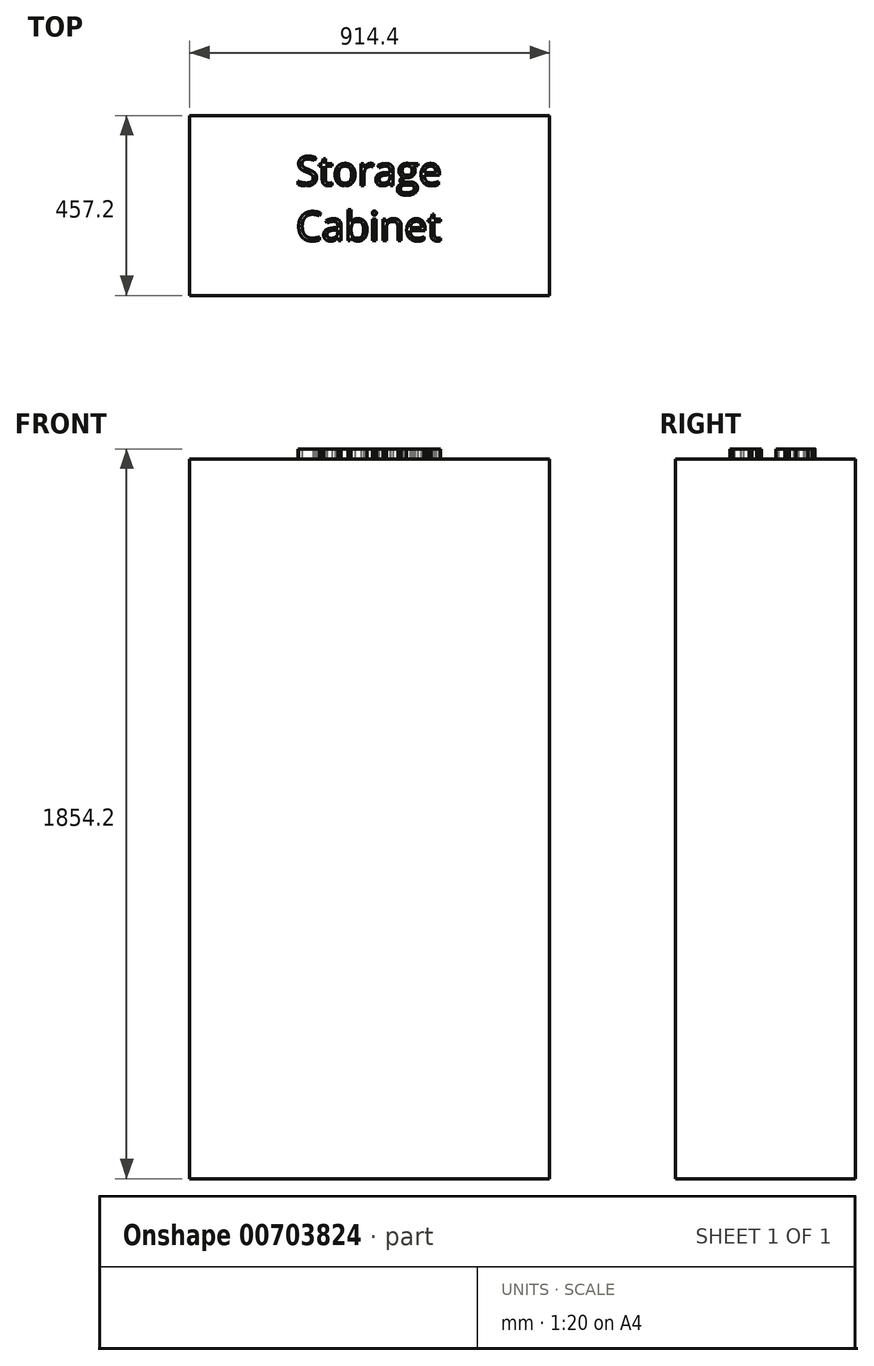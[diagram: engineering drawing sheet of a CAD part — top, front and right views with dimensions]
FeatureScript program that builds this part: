
annotation { "Feature Type Name" : "Feature", "Feature Type Description" : "" }
export const myFeature = defineFeature(function(context is Context, id is Id, definition is map)
    precondition{}
    {
        {
            var Q0;
            Q0=qCreatedBy(makeId("Top.planeOp"),FACE);
            var sketch = newSketch(context, id + "F0", { "sketchPlane" : qUnion([Q0])});
            skLineSegment(sketch, "E0.bottom", {"start": v(457.2, -228.6) * mm, "end": v(-457.2, -228.6) * mm});
            skLineSegment(sketch, "E0.top", {"start": v(457.2, 228.6) * mm, "end": v(-457.2, 228.6) * mm});
            skLineSegment(sketch, "E0.left", {"start": v(457.2, -228.6) * mm, "end": v(457.2, 228.6) * mm});
            skLineSegment(sketch, "E0.right", {"start": v(-457.2, -228.6) * mm, "end": v(-457.2, 228.6) * mm});
            skPoint(sketch, "E0.middle", {"position": v(0, 0) * mm});
            skSolve(sketch);
        }
        {
            var Q0;
            Q0=makeQuery(id+"F0.imprint","IMPRINT",FACE,{"disambiguationData":[TD([[makeQuery(id+"F0.imprint","IMPRINT",EDGE,{"derivedFrom":sQuery(id+"F0.wireOp",EDGE,"E0.bottom")}),-1.0]])]});
            extrude(context, id + "F1", {"entities" : qUnion([Q0]), "depth" : 1828.8 * mm, "offsetDistance" : 25.4 * mm});
        }
        {
            var Q0;
            Q0=makeQuery(id+"F1.opExtrude","CAP_FACE",FACE,{"disambiguationData":[OSD([sQuery(id+"F0.wireOp",EDGE,"E0.bottom"),sQuery(id+"F0.wireOp",EDGE,"E0.top"),sQuery(id+"F0.wireOp",EDGE,"E0.left"),sQuery(id+"F0.wireOp",EDGE,"E0.right")])],"isStart":false});
            var sketch = newSketch(context, id + "F2", { "sketchPlane" : qUnion([Q0])});
            skText(sketch, "E1", { "text": "Storage \nCabinet", "fontName": "OpenSans-Regular.ttf"});
            const initialGuessF2  = {"E1": [-0.18697, 0.05058, 1, 0, 0.07428]};
            skSetInitialGuess(sketch, initialGuessF2);
            skSolve(sketch);
        }
        {
            var Q0;
            Q0 = qSketchRegion(id + "F2", true);
            extrude(context, id + "F3", {"entities" : qUnion([Q0]), "operationType" : NewBodyOperationType.ADD, "depth" : 25.4 * mm, "offsetDistance" : 25.4 * mm});
        }
    });
